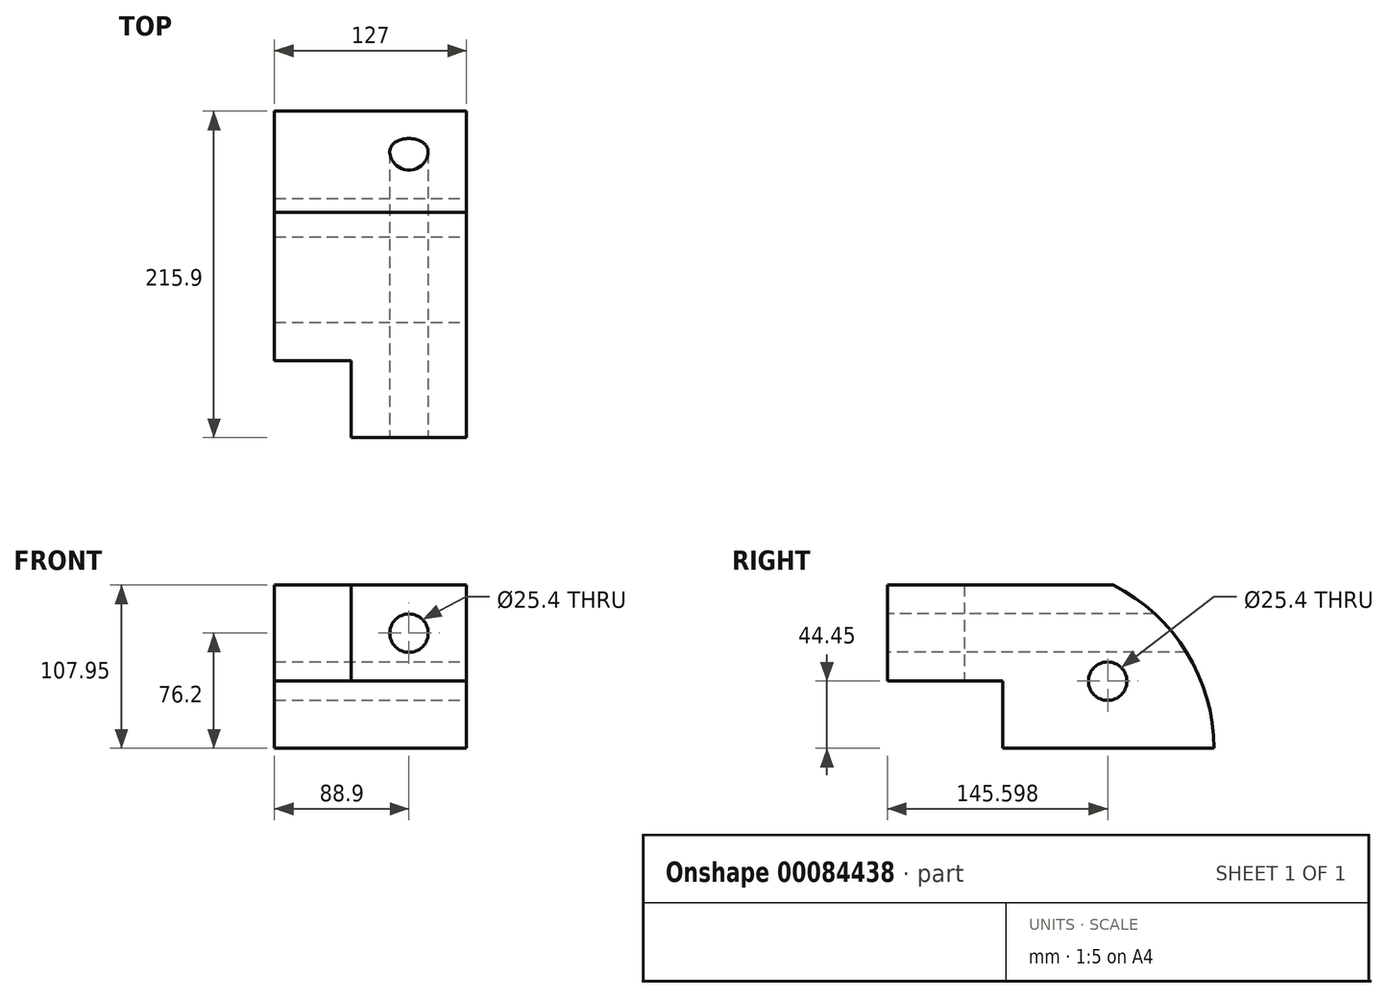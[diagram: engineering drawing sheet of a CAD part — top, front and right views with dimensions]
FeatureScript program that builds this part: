
annotation { "Feature Type Name" : "Feature", "Feature Type Description" : "" }
export const myFeature = defineFeature(function(context is Context, id is Id, definition is map)
    precondition{}
    {
        {
            var Q0;
            Q0=qCreatedBy(makeId("Top.planeOp"),FACE);
            var sketch = newSketch(context, id + "F0", { "sketchPlane" : qUnion([Q0])});
            skLineSegment(sketch, "E0.bottom", {"start": v(0, 0.95) * mm, "end": v(127, 0.95) * mm});
            skLineSegment(sketch, "E0.top", {"start": v(0, 216.85) * mm, "end": v(127, 216.85) * mm});
            skLineSegment(sketch, "E0.left", {"start": v(0, 0.95) * mm, "end": v(0, 216.85) * mm});
            skLineSegment(sketch, "E0.right", {"start": v(127, 0.95) * mm, "end": v(127, 216.85) * mm});
            skSolve(sketch);
        }
        {
            var Q0;
            Q0=makeQuery(id+"F0.imprint","IMPRINT",FACE,{"disambiguationData":[TD([[makeQuery(id+"F0.imprint","IMPRINT",EDGE,{"derivedFrom":sQuery(id+"F0.wireOp",EDGE,"E0.bottom")}),1.0]])]});
            extrude(context, id + "F1", {"entities" : qUnion([Q0]), "depth" : 107.95 * mm});
        }
        {
            var Q0;
            Q0=makeQuery(id+"F1.opExtrude","SWEPT_FACE",FACE,{"disambiguationData":[OSD([sQuery(id+"F0.wireOp",EDGE,"E0.right")])]});
            var sketch = newSketch(context, id + "F2", { "sketchPlane" : qUnion([Q0])});
            skLineSegment(sketch, "E1", {"start": v(216.85, 0) * mm, "end": v(153.35, 0) * mm});
            skLineSegment(sketch, "E2.bottom", {"start": v(0.95, 0) * mm, "end": v(77.15, 0) * mm});
            skLineSegment(sketch, "E2.top", {"start": v(0.95, 44.45) * mm, "end": v(77.15, 44.45) * mm});
            skLineSegment(sketch, "E2.left", {"start": v(0.95, 0) * mm, "end": v(0.95, 44.45) * mm});
            skLineSegment(sketch, "E2.right", {"start": v(77.15, 0) * mm, "end": v(77.15, 44.45) * mm});
            skLineSegment(sketch, "E3.bottom", {"start": v(216.85, 0) * mm, "end": v(146.55, 0) * mm});
            skLineSegment(sketch, "E3.top", {"start": v(216.85, 44.45) * mm, "end": v(146.55, 44.45) * mm});
            skLineSegment(sketch, "E3.left", {"start": v(216.85, 0) * mm, "end": v(216.85, 44.45) * mm});
            skLineSegment(sketch, "E3.right", {"start": v(146.55, 0) * mm, "end": v(146.55, 44.45) * mm});
            skCircle(sketch, "E4", {"center": v(146.55, 44.45) * mm, "radius": 12.7 * mm});
            skSolve(sketch);
        }
        {
            var Q0;
            Q0=makeQuery(id+"F1.opExtrude","SWEPT_FACE",FACE,{"disambiguationData":[OSD([sQuery(id+"F0.wireOp",EDGE,"E0.bottom")])]});
            var sketch = newSketch(context, id + "F3", { "sketchPlane" : qUnion([Q0])});
            skLineSegment(sketch, "E5.bottom", {"start": v(127, 107.95) * mm, "end": v(50.8, 107.95) * mm});
            skLineSegment(sketch, "E5.top", {"start": v(127, 44.45) * mm, "end": v(50.8, 44.45) * mm});
            skLineSegment(sketch, "E5.left", {"start": v(127, 107.95) * mm, "end": v(127, 44.45) * mm});
            skLineSegment(sketch, "E5.right", {"start": v(50.8, 107.95) * mm, "end": v(50.8, 44.45) * mm});
            skLineSegment(sketch, "E6.bottom", {"start": v(127, 107.95) * mm, "end": v(88.9, 107.95) * mm});
            skLineSegment(sketch, "E6.top", {"start": v(127, 76.2) * mm, "end": v(88.9, 76.2) * mm});
            skLineSegment(sketch, "E6.left", {"start": v(127, 107.95) * mm, "end": v(127, 76.2) * mm});
            skLineSegment(sketch, "E6.right", {"start": v(88.9, 107.95) * mm, "end": v(88.9, 76.2) * mm});
            skCircle(sketch, "E7", {"center": v(88.9, 76.2) * mm, "radius": 12.7 * mm});
            skLineSegment(sketch, "E8.bottom", {"start": v(50.8, 44.45) * mm, "end": v(0, 44.45) * mm});
            skLineSegment(sketch, "E8.top", {"start": v(50.8, 0) * mm, "end": v(0, 0) * mm});
            skLineSegment(sketch, "E8.left", {"start": v(50.8, 44.45) * mm, "end": v(50.8, 0) * mm});
            skLineSegment(sketch, "E8.right", {"start": v(0, 44.45) * mm, "end": v(0, 0) * mm});
            skLineSegment(sketch, "E9.bottom", {"start": v(50.8, 44.45) * mm, "end": v(127, 44.45) * mm});
            skLineSegment(sketch, "E9.top", {"start": v(50.8, 0) * mm, "end": v(127, 0) * mm});
            skLineSegment(sketch, "E9.right", {"start": v(127, 44.45) * mm, "end": v(127, 0) * mm});
            skLineSegment(sketch, "E10.top", {"start": v(50.8, 107.95) * mm, "end": v(0, 107.95) * mm});
            skLineSegment(sketch, "E10.left", {"start": v(50.8, 44.45) * mm, "end": v(50.8, 107.95) * mm});
            skLineSegment(sketch, "E10.right", {"start": v(0, 44.45) * mm, "end": v(0, 107.95) * mm});
            skSolve(sketch);
        }
        {
            var Q0;
            {var subQ4=sQuery(id+"F3.wireOp",EDGE,"E5.top");Q0=makeQuery(id+"F3.imprint","IMPRINT",FACE,{"disambiguationData":[TD([[makeQuery(id+"F3.imprint","IMPRINT",EDGE,{"derivedFrom":subQ4}),1.0]])]});}
            var Q1;
            Q1=makeQuery(id+"F3.imprint","IMPRINT",FACE,{"disambiguationData":[TD([[makeQuery(id+"F3.imprint","IMPRINT",EDGE,{"derivedFrom":sQuery(id+"F3.wireOp",EDGE,"E9.bottom")}),-1.0]])]});
            var Q2;
            Q2=makeQuery(id+"F3.imprint","IMPRINT",FACE,{"disambiguationData":[TD([[makeQuery(id+"F3.imprint","IMPRINT",EDGE,{"derivedFrom":sQuery(id+"F3.wireOp",EDGE,"E8.top")}),1.0]])]});
            extrude(context, id + "F4", {"entities" : qUnion([Q0, Q1, Q2]), "operationType" : NewBodyOperationType.REMOVE, "oppositeDirection" : true, "depth" : 76.2 * mm});
        }
        {
            var Q0;
            Q0=sQuery(id+"F2.wireOp",VERTEX,"E4.center");
            var Q1;
            Q1=makeQuery(id+"F1.opExtrude","SWEPT_BODY",BODY,{"disambiguationData":[OSD([sQuery(id+"F0.wireOp",EDGE,"E0.bottom"),sQuery(id+"F0.wireOp",EDGE,"E0.top"),sQuery(id+"F0.wireOp",EDGE,"E0.left"),sQuery(id+"F0.wireOp",EDGE,"E0.right")])]});
            hole(context, id + "F5", {"style" : HoleStyle.SIMPLE, "endStyle" : HoleEndStyle.THROUGH, "holeDiameter" : 25.4 * mm, "locations" : qUnion([Q0]), "scope" : qUnion([Q1]), "isTappedThrough" : true});
        }
        {
            var Q0;
            Q0=makeQuery(id+"F1.opExtrude","SWEPT_FACE",FACE,{"disambiguationData":[OSD([sQuery(id+"F0.wireOp",EDGE,"E0.right")])]});
            var sketch = newSketch(context, id + "F6", { "sketchPlane" : qUnion([Q0])});
            skLineSegment(sketch, "E11", {"start": v(216.85, 0) * mm, "end": v(96.2, 0) * mm});
            skArc(sketch, "E12", {"start": v(216.85, 0) * mm, "mid": v(198.8, 63.47) * mm, "end": v(150.08, 107.95) * mm});
            skSolve(sketch);
        }
        {
            var Q0;
            {var subQ0=sQuery(id+"F6.wireOp",EDGE,"E12");Q0=makeQuery(id+"F6.imprint","IMPRINT",FACE,{"disambiguationData":[TD([[makeQuery(id+"F6.imprint","IMPRINT",EDGE,{"derivedFrom":subQ0}),-1.0]])]});}
            extrude(context, id + "F7", {"entities" : qUnion([Q0]), "operationType" : NewBodyOperationType.REMOVE, "endBound" : BoundingType.THROUGH_ALL, "oppositeDirection" : true, "depth" : 25.4 * mm});
        }
        {
            var Q0;
            Q0=makeQuery(id+"F1.opExtrude","SWEPT_FACE",FACE,{"disambiguationData":[OSD([sQuery(id+"F0.wireOp",EDGE,"E0.bottom")])]});
            var sketch = newSketch(context, id + "F8", { "sketchPlane" : qUnion([Q0])});
            skLineSegment(sketch, "E13.bottom", {"start": v(127, 107.95) * mm, "end": v(88.9, 107.95) * mm});
            skLineSegment(sketch, "E13.top", {"start": v(127, 76.2) * mm, "end": v(88.9, 76.2) * mm});
            skLineSegment(sketch, "E13.left", {"start": v(127, 107.95) * mm, "end": v(127, 76.2) * mm});
            skLineSegment(sketch, "E13.right", {"start": v(88.9, 107.95) * mm, "end": v(88.9, 76.2) * mm});
            skCircle(sketch, "E14", {"center": v(88.9, 76.2) * mm, "radius": 12.7 * mm});
            skSolve(sketch);
        }
        {
            var Q0;
            Q0=sQuery(id+"F8.wireOp",VERTEX,"E13.top.end");
            var Q1;
            Q1=makeQuery(id+"F1.opExtrude","SWEPT_BODY",BODY,{"disambiguationData":[OSD([sQuery(id+"F0.wireOp",EDGE,"E0.bottom"),sQuery(id+"F0.wireOp",EDGE,"E0.top"),sQuery(id+"F0.wireOp",EDGE,"E0.left"),sQuery(id+"F0.wireOp",EDGE,"E0.right")])]});
            hole(context, id + "F9", {"style" : HoleStyle.SIMPLE, "endStyle" : HoleEndStyle.THROUGH, "holeDiameter" : 25.4 * mm, "locations" : qUnion([Q0]), "scope" : qUnion([Q1]), "isTappedThrough" : true});
        }
        {
            var Q0;
            Q0=makeQuery(id+"F3.imprint","IMPRINT",FACE,{"disambiguationData":[TD([[makeQuery(id+"F3.imprint","IMPRINT",EDGE,{"derivedFrom":sQuery(id+"F3.wireOp",EDGE,"E8.bottom")}),-1.0]])]});
            extrude(context, id + "F10", {"entities" : qUnion([Q0]), "operationType" : NewBodyOperationType.REMOVE, "oppositeDirection" : true, "depth" : 50.8 * mm});
        }
    });
